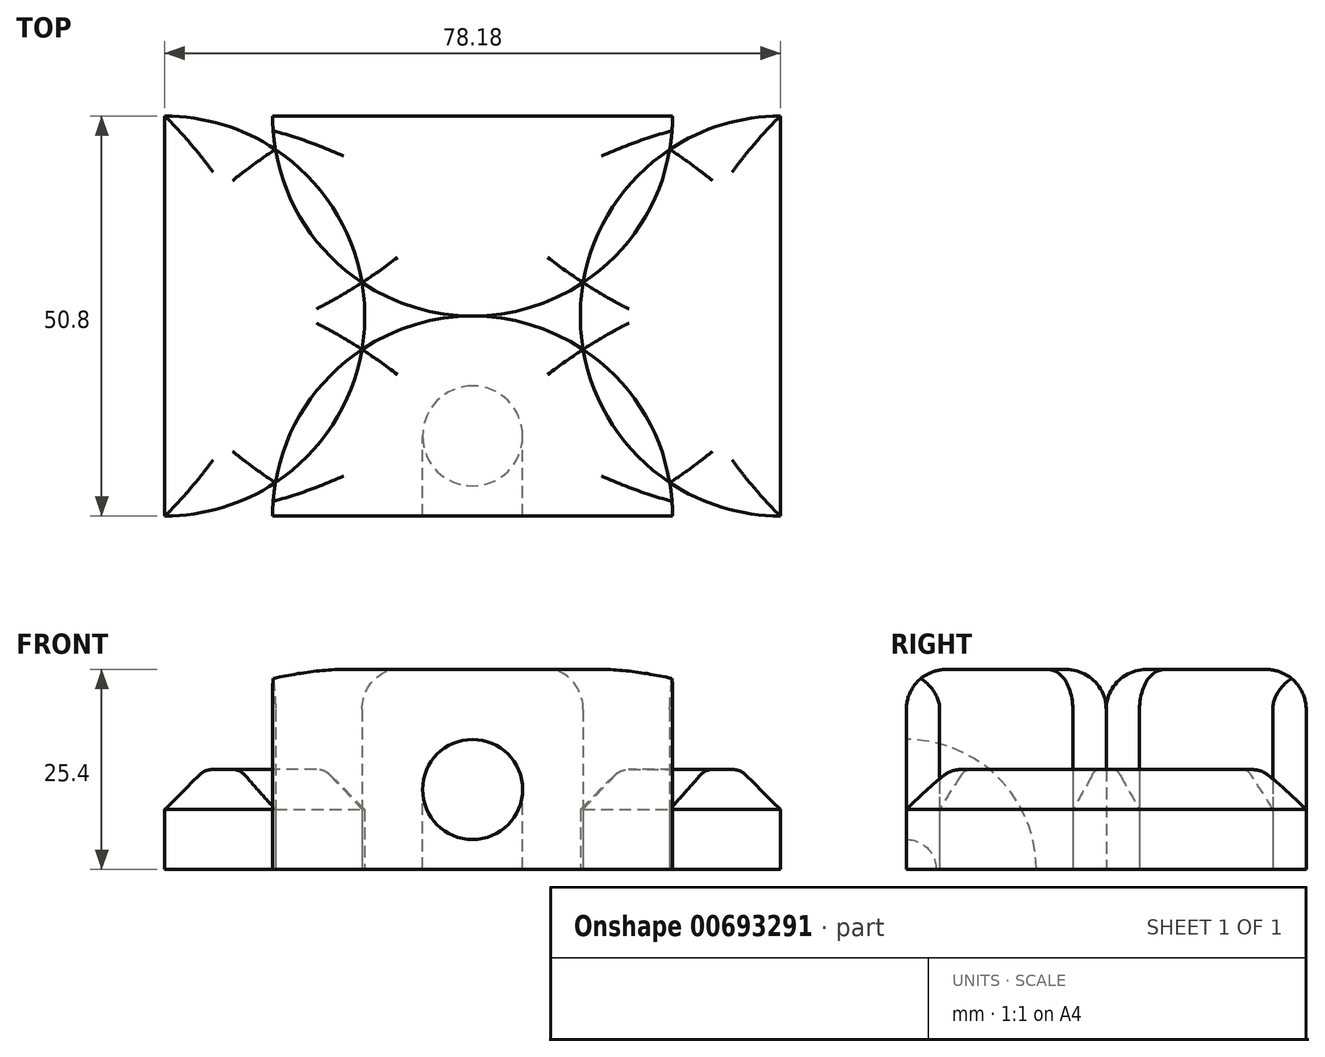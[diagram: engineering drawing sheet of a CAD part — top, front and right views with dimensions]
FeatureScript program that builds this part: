
annotation { "Feature Type Name" : "Feature", "Feature Type Description" : "" }
export const myFeature = defineFeature(function(context is Context, id is Id, definition is map)
    precondition{}
    {
        {
            var Q0;
            Q0=qCreatedBy(makeId("Top.planeOp"),FACE);
            var sketch = newSketch(context, id + "F0", { "sketchPlane" : qUnion([Q0])});
            skLineSegment(sketch, "E0.bottom", {"start": v(0, 0) * mm, "end": v(78.18, 0) * mm});
            skLineSegment(sketch, "E0.top", {"start": v(0, 50.8) * mm, "end": v(78.18, 50.8) * mm});
            skLineSegment(sketch, "E0.left", {"start": v(0, 0) * mm, "end": v(0, 50.8) * mm});
            skLineSegment(sketch, "E0.right", {"start": v(78.18, 0) * mm, "end": v(78.18, 50.8) * mm});
            skCircle(sketch, "E1", {"center": v(78.18, 25.4) * mm, "radius": 25.4 * mm});
            skCircle(sketch, "E2", {"center": v(0, 25.4) * mm, "radius": 25.4 * mm});
            skCircle(sketch, "E3", {"center": v(39.1, 50.8) * mm, "radius": 25.4 * mm});
            skPoint(sketch, "E3.perimeterSnap0", {"position": v(39.1, 50.8) * mm});
            skCircle(sketch, "E4", {"center": v(39.1, 0) * mm, "radius": 25.4 * mm});
            skSolve(sketch);
        }
        {
            var Q0;
            {var subQ0=sQuery(id+"F0.wireOp",EDGE,"E3");var subQ1=sQuery(id+"F0.wireOp",EDGE,"E0.top");var subQ2=makeQuery(id+"F0.imprint","INTERSECT",VERTEX,{"disambiguationData":[OD(0.0)],"derivedFrom":[subQ1,subQ0]});Q0=makeQuery(id+"F0.imprint","IMPRINT",FACE,{"disambiguationData":[TD([[makeQuery(id+"F0.imprint","IMPRINT",EDGE,{"disambiguationData":[TD([[subQ2,-1.0]])],"derivedFrom":subQ1}),-1.0]])]});}
            extrude(context, id + "F1", {"entities" : qUnion([Q0]), "depth" : 25.4 * mm, "offsetDistance" : 25.4 * mm});
        }
        {
            var Q0;
            {var subQ0=sQuery(id+"F0.wireOp",EDGE,"E4");var subQ1=sQuery(id+"F0.wireOp",EDGE,"E0.bottom");var subQ10=makeQuery(id+"F0.imprint","INTERSECT",VERTEX,{"disambiguationData":[OD(0.0)],"derivedFrom":[subQ1,subQ0]});Q0=makeQuery(id+"F0.imprint","IMPRINT",FACE,{"disambiguationData":[TD([[makeQuery(id+"F0.imprint","IMPRINT",EDGE,{"disambiguationData":[TD([[subQ10,-1.0]])],"derivedFrom":subQ1}),1.0]])]});}
            extrude(context, id + "F2", {"entities" : qUnion([Q0]), "operationType" : NewBodyOperationType.ADD, "depth" : 25.4 * mm, "offsetDistance" : 25.4 * mm});
        }
        {
            var Q0;
            Q0=makeQuery(id+"F2.opExtrude","CAP_FACE",FACE,{"disambiguationData":[OSD([sQuery(id+"F0.wireOp",EDGE,"E0.bottom"),sQuery(id+"F0.wireOp",EDGE,"E1"),sQuery(id+"F0.wireOp",EDGE,"E2"),sQuery(id+"F0.wireOp",EDGE,"E4")])],"isStart":false});
            var Q1;
            Q1=makeQuery(id+"F1.opExtrude","CAP_FACE",FACE,{"disambiguationData":[OSD([sQuery(id+"F0.wireOp",EDGE,"E0.top"),sQuery(id+"F0.wireOp",EDGE,"E1"),sQuery(id+"F0.wireOp",EDGE,"E2"),sQuery(id+"F0.wireOp",EDGE,"E3")])],"isStart":false});
            fillet(context, id + "F3", {"entities" : qUnion([Q0, Q1]), "radius" : 5.08 * mm, "tangentPropagation" : true, "allowEdgeOverflow" : false});
        }
        {
            var Q0;
            {var subQ5=sQuery(id+"F0.wireOp",EDGE,"E0.left");Q0=makeQuery(id+"F0.imprint","IMPRINT",FACE,{"disambiguationData":[TD([[makeQuery(id+"F0.imprint","IMPRINT",EDGE,{"derivedFrom":subQ5}),-1.0]])]});}
            var Q1;
            {var subQ5=sQuery(id+"F0.wireOp",EDGE,"E0.right");Q1=makeQuery(id+"F0.imprint","IMPRINT",FACE,{"disambiguationData":[TD([[makeQuery(id+"F0.imprint","IMPRINT",EDGE,{"derivedFrom":subQ5}),1.0]])]});}
            extrude(context, id + "F4", {"entities" : qUnion([Q0, Q1]), "depth" : 12.7 * mm, "offsetDistance" : 25.4 * mm});
        }
        {
            var Q0;
            Q0=makeQuery(id+"F4.opExtrude","CAP_FACE",FACE,{"disambiguationData":[OSD([sQuery(id+"F0.wireOp",EDGE,"E0.right"),sQuery(id+"F0.wireOp",EDGE,"E1"),sQuery(id+"F0.wireOp",EDGE,"E3"),sQuery(id+"F0.wireOp",EDGE,"E4")])],"isStart":false});
            var Q1;
            Q1=makeQuery(id+"F4.opExtrude","CAP_FACE",FACE,{"disambiguationData":[OSD([sQuery(id+"F0.wireOp",EDGE,"E0.left"),sQuery(id+"F0.wireOp",EDGE,"E2"),sQuery(id+"F0.wireOp",EDGE,"E3"),sQuery(id+"F0.wireOp",EDGE,"E4")])],"isStart":false});
            chamfer(context, id + "F5", {"entities" : qUnion([Q0, Q1]), "width" : 5.08 * mm, "tangentPropagation" : true});
        }
        {
            var Q0;
            Q0=makeQuery(id+"F4.opExtrude","CAP_FACE",FACE,{"disambiguationData":[OSD([sQuery(id+"F0.wireOp",EDGE,"E0.left"),sQuery(id+"F0.wireOp",EDGE,"E2"),sQuery(id+"F0.wireOp",EDGE,"E3"),sQuery(id+"F0.wireOp",EDGE,"E4")])],"isStart":false});
            fillet(context, id + "F6", {"entities" : qUnion([Q0]), "radius" : 2.54 * mm, "tangentPropagation" : true, "allowEdgeOverflow" : false});
        }
        {
            var Q0;
            Q0=makeQuery(id+"F4.opExtrude","CAP_FACE",FACE,{"disambiguationData":[OSD([sQuery(id+"F0.wireOp",EDGE,"E0.right"),sQuery(id+"F0.wireOp",EDGE,"E1"),sQuery(id+"F0.wireOp",EDGE,"E3"),sQuery(id+"F0.wireOp",EDGE,"E4")])],"isStart":false});
            fillet(context, id + "F7", {"entities" : qUnion([Q0]), "radius" : 2.54 * mm, "tangentPropagation" : true, "allowEdgeOverflow" : false});
        }
        {
            var Q0;
            Q0=makeQuery(id+"F2.opExtrude","SWEPT_FACE",FACE,{"disambiguationData":[OSD([sQuery(id+"F0.wireOp",EDGE,"E0.bottom")])]});
            var sketch = newSketch(context, id + "F8", { "sketchPlane" : qUnion([Q0])});
            skLineSegment(sketch, "E5", {"start": v(13.7, 10.16) * mm, "end": v(64.5, 10.16) * mm, "construction": true});
            skLineSegment(sketch, "E6", {"start": v(39.1, 20.32) * mm, "end": v(39.1, 0) * mm, "construction": true});
            skCircle(sketch, "E7", {"center": v(39.1, 10.16) * mm, "radius": 6.35 * mm});
            skSolve(sketch);
        }
        {
            var Q0;
            Q0=makeQuery(id+"F8.imprint","IMPRINT",FACE,{"disambiguationData":[TD([[makeQuery(id+"F8.imprint","IMPRINT",EDGE,{"derivedFrom":sQuery(id+"F8.wireOp",EDGE,"E7")}),1.0]])]});
            var Q1;
            Q1=sQuery(id+"F8.wireOp",EDGE,"E7");
            var Q2;
            Q2=sQuery(id+"F0.wireOp",EDGE,"E0.bottom");
            revolve(context, id + "F9", {"operationType" : NewBodyOperationType.REMOVE, "entities" : qUnion([Q0]), "surfaceEntities" : qUnion([Q1]), "axis" : qUnion([Q2]), "revolveType" : RevolveType.FULL, "oppositeDirection" : true});
        }
    });
